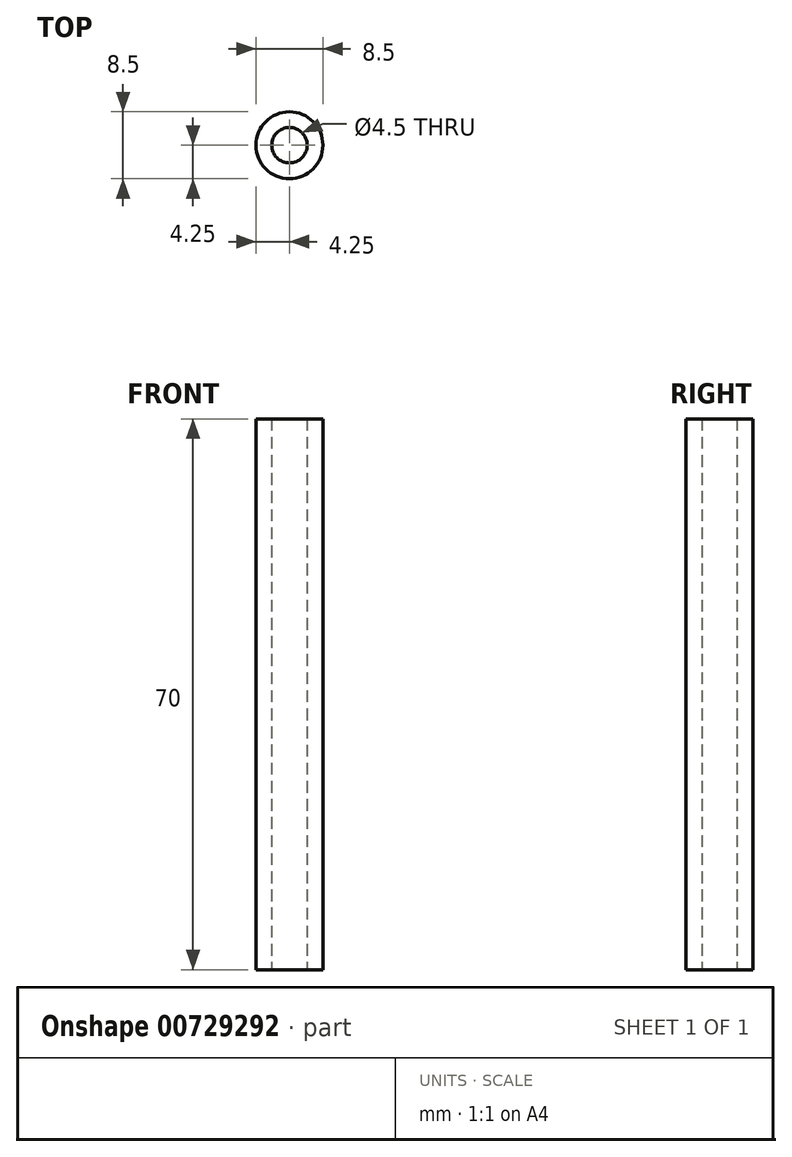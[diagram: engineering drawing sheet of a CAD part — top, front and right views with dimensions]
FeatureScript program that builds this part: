
annotation { "Feature Type Name" : "Feature", "Feature Type Description" : "" }
export const myFeature = defineFeature(function(context is Context, id is Id, definition is map)
    precondition{}
    {
        {
            var Q0;
            Q0=qCreatedBy(makeId("Top.planeOp"),FACE);
            var sketch = newSketch(context, id + "F0", { "sketchPlane" : qUnion([Q0])});
            skCircle(sketch, "E0", {"center": v(0, 0) * mm, "radius": 2.25 * mm});
            skCircle(sketch, "E1.0", {"center": v(0, 0) * mm, "radius": 4.25 * mm});
            skSolve(sketch);
        }
        {
            var Q0;
            Q0=makeQuery(id+"F0.imprint","IMPRINT",FACE,{"disambiguationData":[TD([[makeQuery(id+"F0.imprint","IMPRINT",EDGE,{"derivedFrom":sQuery(id+"F0.wireOp",EDGE,"E0")}),-1.0]])]});
            extrude(context, id + "F1", {"entities" : qUnion([Q0]), "depth" : 70 * mm, "offsetDistance" : 25 * mm});
        }
    });
